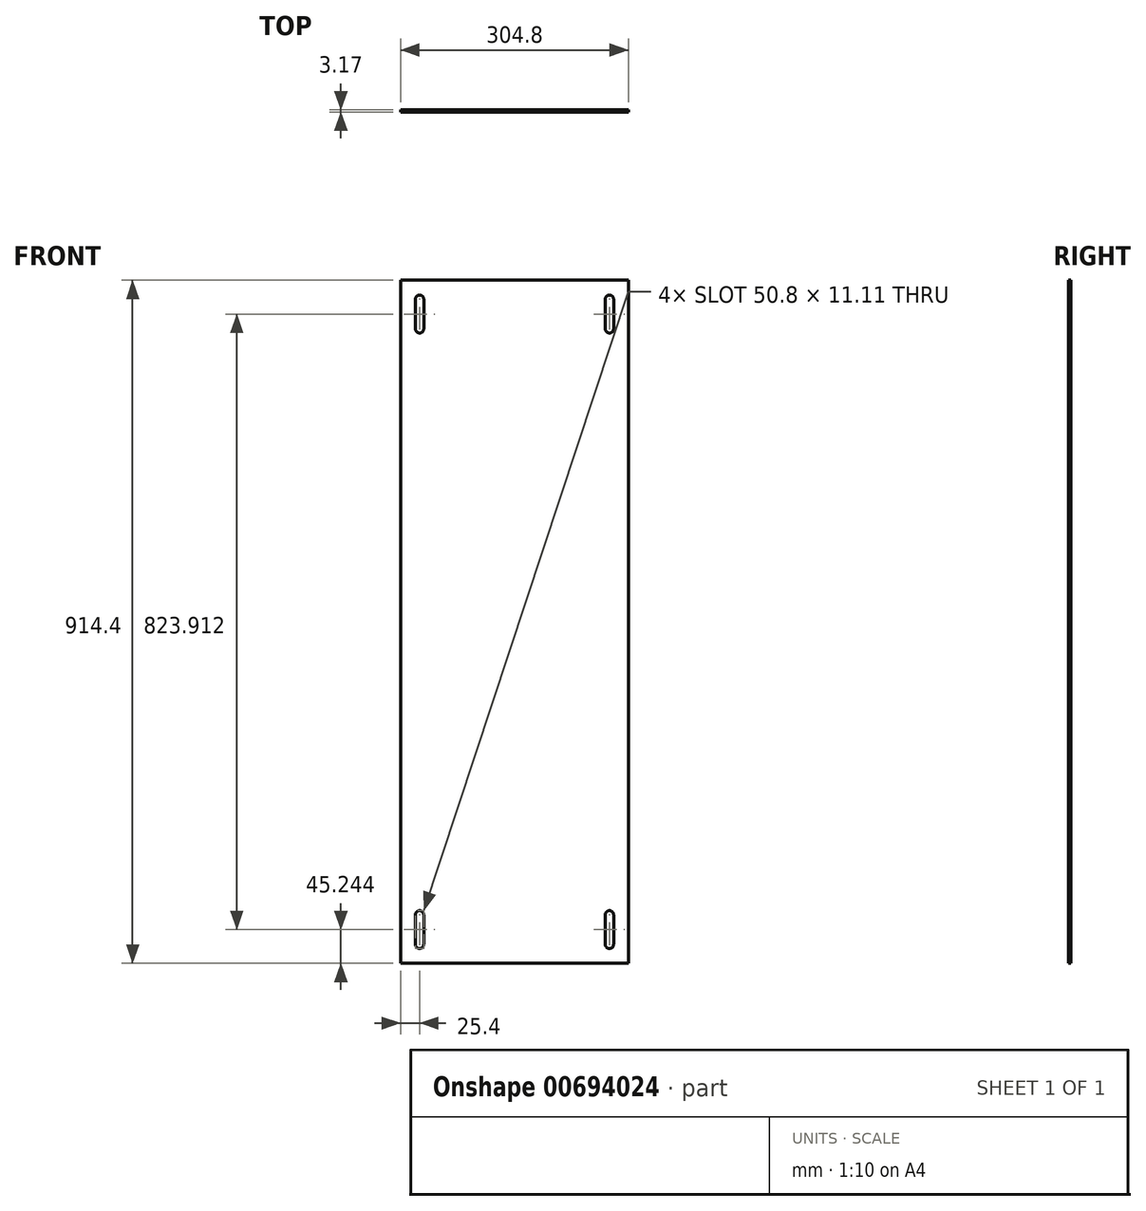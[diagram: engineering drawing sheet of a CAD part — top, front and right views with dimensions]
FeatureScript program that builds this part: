
annotation { "Feature Type Name" : "Feature", "Feature Type Description" : "" }
export const myFeature = defineFeature(function(context is Context, id is Id, definition is map)
    precondition{}
    {
        {
            var Q0;
            Q0=qCreatedBy(makeId("Front.planeOp"),FACE);
            var sketch = newSketch(context, id + "F0", { "sketchPlane" : qUnion([Q0])});
            skLineSegment(sketch, "E0.bottom", {"start": v(-152.4, 457.2) * mm, "end": v(152.4, 457.2) * mm});
            skLineSegment(sketch, "E0.top", {"start": v(-152.4, -457.2) * mm, "end": v(152.4, -457.2) * mm});
            skLineSegment(sketch, "E0.left", {"start": v(-152.4, 457.2) * mm, "end": v(-152.4, -457.2) * mm});
            skLineSegment(sketch, "E0.right", {"start": v(152.4, 457.2) * mm, "end": v(152.4, -457.2) * mm});
            skLineSegment(sketch, "E1", {"start": v(-152.4, 0) * mm, "end": v(152.4, 0) * mm, "construction": true});
            skArc(sketch, "E2", {"start": v(-121.44, 431.8) * mm, "mid": v(-127, 437.36) * mm, "end": v(-132.56, 431.8) * mm});
            skArc(sketch, "E3", {"start": v(-132.56, 392.11) * mm, "mid": v(-127, 386.56) * mm, "end": v(-121.44, 392.11) * mm});
            skLineSegment(sketch, "E4", {"start": v(-132.56, 431.8) * mm, "end": v(-132.56, 392.11) * mm});
            skLineSegment(sketch, "E5", {"start": v(-121.44, 431.8) * mm, "end": v(-121.44, 392.11) * mm});
            skLineSegment(sketch, "E6.MirrorCS", {"start": v(132.56, 431.8) * mm, "end": v(132.56, 392.11) * mm});
            skLineSegment(sketch, "E7.MirrorCS", {"start": v(121.44, 431.8) * mm, "end": v(121.44, 392.11) * mm});
            skArc(sketch, "E8.MirrorCS", {"start": v(132.56, 392.11) * mm, "mid": v(127, 386.56) * mm, "end": v(121.44, 392.11) * mm});
            skArc(sketch, "E9.MirrorCS", {"start": v(121.44, 431.8) * mm, "mid": v(127, 437.36) * mm, "end": v(132.56, 431.8) * mm});
            skArc(sketch, "E10.MirrorCS", {"start": v(121.44, -431.8) * mm, "mid": v(127, -437.36) * mm, "end": v(132.56, -431.8) * mm});
            skArc(sketch, "E11.MirrorCS", {"start": v(132.56, -392.11) * mm, "mid": v(127, -386.56) * mm, "end": v(121.44, -392.11) * mm});
            skLineSegment(sketch, "E12.MirrorCS", {"start": v(121.44, -431.8) * mm, "end": v(121.44, -392.11) * mm});
            skLineSegment(sketch, "E13.MirrorCS", {"start": v(132.56, -431.8) * mm, "end": v(132.56, -392.11) * mm});
            skLineSegment(sketch, "E14.MirrorCS", {"start": v(-132.56, -431.8) * mm, "end": v(-132.56, -392.11) * mm});
            skLineSegment(sketch, "E15.MirrorCS", {"start": v(-121.44, -431.8) * mm, "end": v(-121.44, -392.11) * mm});
            skArc(sketch, "E16.MirrorCS", {"start": v(-121.44, -431.8) * mm, "mid": v(-127, -437.36) * mm, "end": v(-132.56, -431.8) * mm});
            skArc(sketch, "E17.MirrorCS", {"start": v(-132.56, -392.11) * mm, "mid": v(-127, -386.56) * mm, "end": v(-121.44, -392.11) * mm});
            skSolve(sketch);
        }
        {
            var Q0;
            Q0=makeQuery(id+"F0.imprint","IMPRINT",FACE,{"disambiguationData":[TD([[makeQuery(id+"F0.imprint","IMPRINT",EDGE,{"derivedFrom":sQuery(id+"F0.wireOp",EDGE,"E0.bottom")}),-1.0]])]});
            extrude(context, id + "F1", {"entities" : qUnion([Q0]), "depth" : 3.17 * mm, "offsetDistance" : 25.4 * mm});
        }
    });
